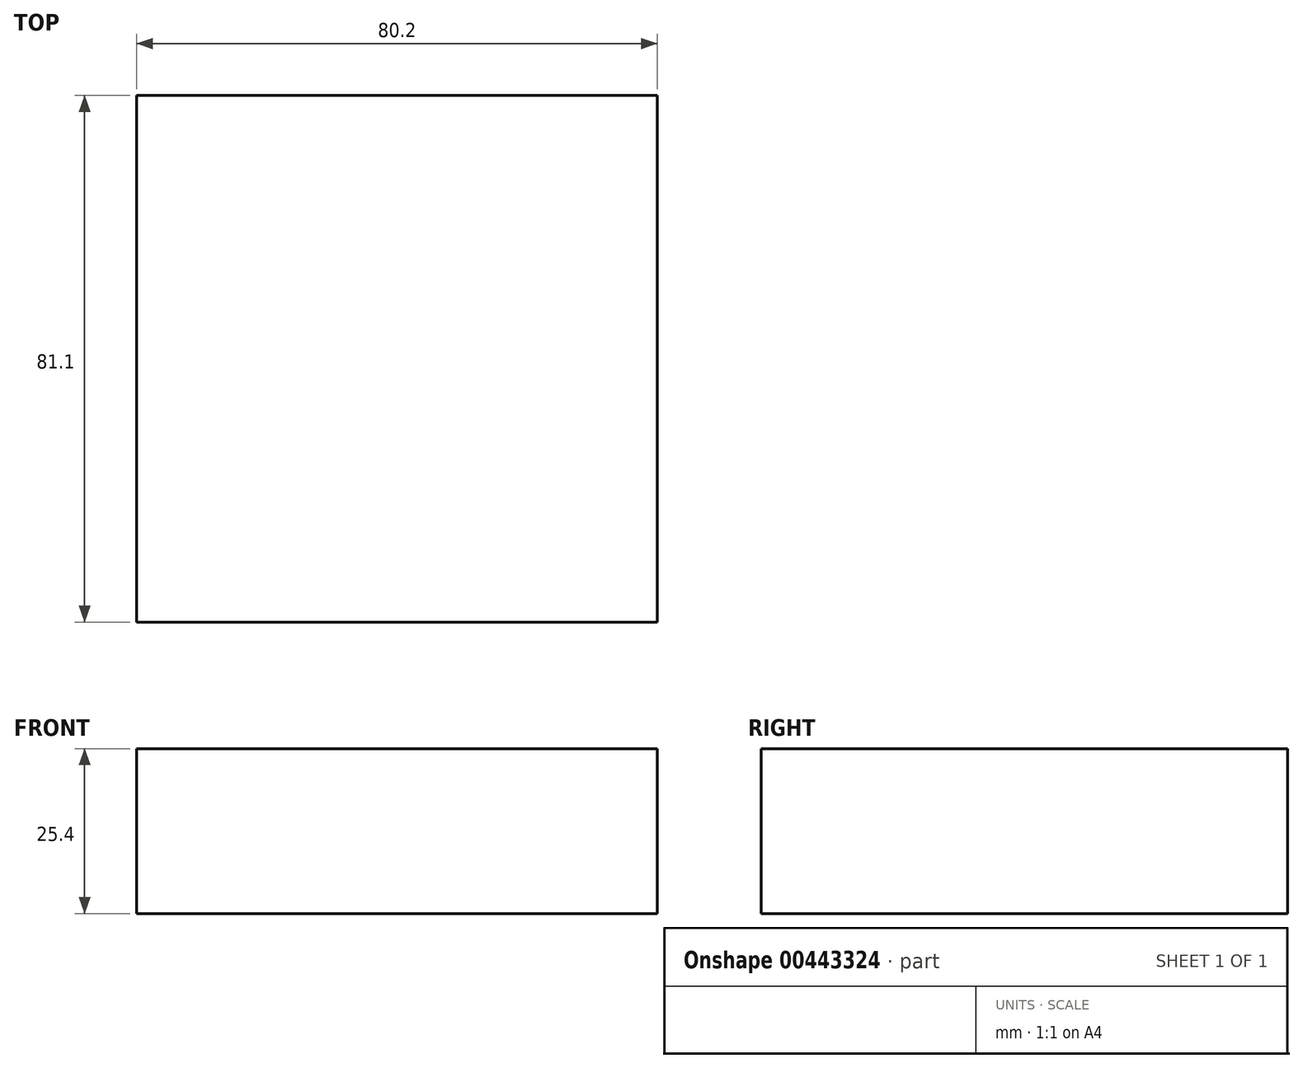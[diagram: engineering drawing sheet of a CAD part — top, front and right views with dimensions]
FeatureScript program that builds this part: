
annotation { "Feature Type Name" : "Feature", "Feature Type Description" : "" }
export const myFeature = defineFeature(function(context is Context, id is Id, definition is map)
    precondition{}
    {
        {
            var Q0;
            Q0=qCreatedBy(makeId("Top.planeOp"),FACE);
            var sketch = newSketch(context, id + "F0", { "sketchPlane" : qUnion([Q0])});
            skLineSegment(sketch, "E0.bottom", {"start": v(40.1, 40.55) * mm, "end": v(-40.1, 40.55) * mm});
            skLineSegment(sketch, "E0.top", {"start": v(40.1, -40.55) * mm, "end": v(-40.1, -40.55) * mm});
            skLineSegment(sketch, "E0.left", {"start": v(40.1, 40.55) * mm, "end": v(40.1, -40.55) * mm});
            skLineSegment(sketch, "E0.right", {"start": v(-40.1, 40.55) * mm, "end": v(-40.1, -40.55) * mm});
            skPoint(sketch, "E0.middle", {"position": v(0, 0) * mm});
            skSolve(sketch);
        }
        {
            var Q0;
            Q0 = qSketchRegion(id + "F0", true);
            extrude(context, id + "F1", {"entities" : qUnion([Q0]), "depth" : 25.4 * mm});
        }
    });
